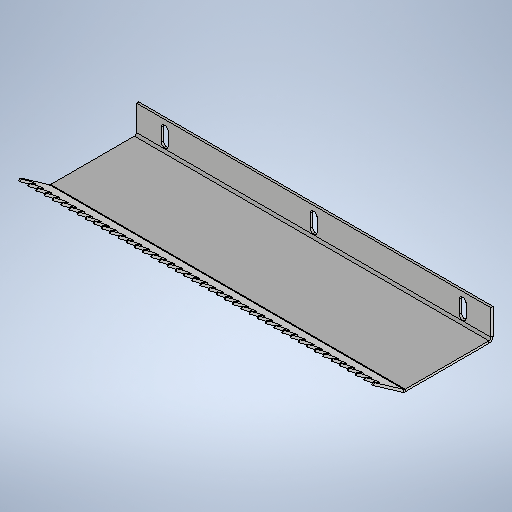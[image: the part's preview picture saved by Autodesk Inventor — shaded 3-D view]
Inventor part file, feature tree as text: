
AUTODESK INVENTOR PART (.ipt)
format: ipt  version: 2025.1 (Build 291241020, 241B)  size: 603,648 bytes
history: native  units: mm
features: sheet_metal_op x7, other x7, sketch x6, pattern_linear x3, projected_geometry x2
ambient origin geometry x8: Origin, YZ Plane, XZ Plane, XY Plane, X Axis, Y Axis, Z Axis, Center Point
bodies: Solid1 (feature_tree)
feature tree (25):
  sheet_metal_op  "Face1"
  pattern_linear  "Rectangular Pattern1"  Count1=12  [1 undecoded]
  sheet_metal_op  "Flange3"
  pattern_linear  "Rectangular Pattern2"  Spacing1=0.0mm  [1 undecoded]
  sheet_metal_op  "Flange4"
  pattern_linear  "Rectangular Pattern3"  Count1=43 Spacing1=11.0mm
  sketch  "Sketch1"  dims[d0=476.0mm d1=120.0mm]
  other  "Plate1"
  sketch  "Sketch6"  dims[d2=3.0mm]
  projected_geometry  "Projected Loop1"
  sketch  "Sketch7"  dims[d33=10.0mm]
  other  "Plate4"
  sheet_metal_op  "Bend3"
  sheet_metal_op  "Corner3"
  sketch  "Sketch8"  dims[d34=6.981317mm]
  sketch  "Sketch9"  dims[d35=3.0mm]
  other  "Plate5"
  sheet_metal_op  "Bend4"
  sheet_metal_op  "Corner4"
  sketch  "Sketch10"  dims[d36=3.0mm d37=0.0mm d38=430.0mm d40=11.0mm d41=3.0mm d42=1.5mm d43=6.0mm d44=2.75mm d45=40.0mm d46=90.0deg d47=2.75mm d48=12.0mm d49=3.0mm d50=2.75mm d51=9.0mm d52=11.0mm d53=18.0mm d54=3.0mm d55=0.0mm d56=30.0mm d58=200.0mm d59=3.0mm d60=1.5mm d61=6.0mm d62=2.75mm d63=50.0mm d64=6.108652mm d65=2.75mm d66=12.0mm d67=3.0mm d68=2.75mm d72=3.0mm d73=15.0mm d74=3.0mm d75=0.0mm d76=430.0mm d78=11.0mm d79=10.0mm]
  projected_geometry  "Projected Loop2"
  other  "Cut1"
  other  "Cut2"
  other  "Cut3"
  other  "Definition1"
note: 2 required parameter values undecoded (feature->parameter linkage not recoverable at this tier; creation-order binding heuristic only, values carry confidence <= 0.55)
